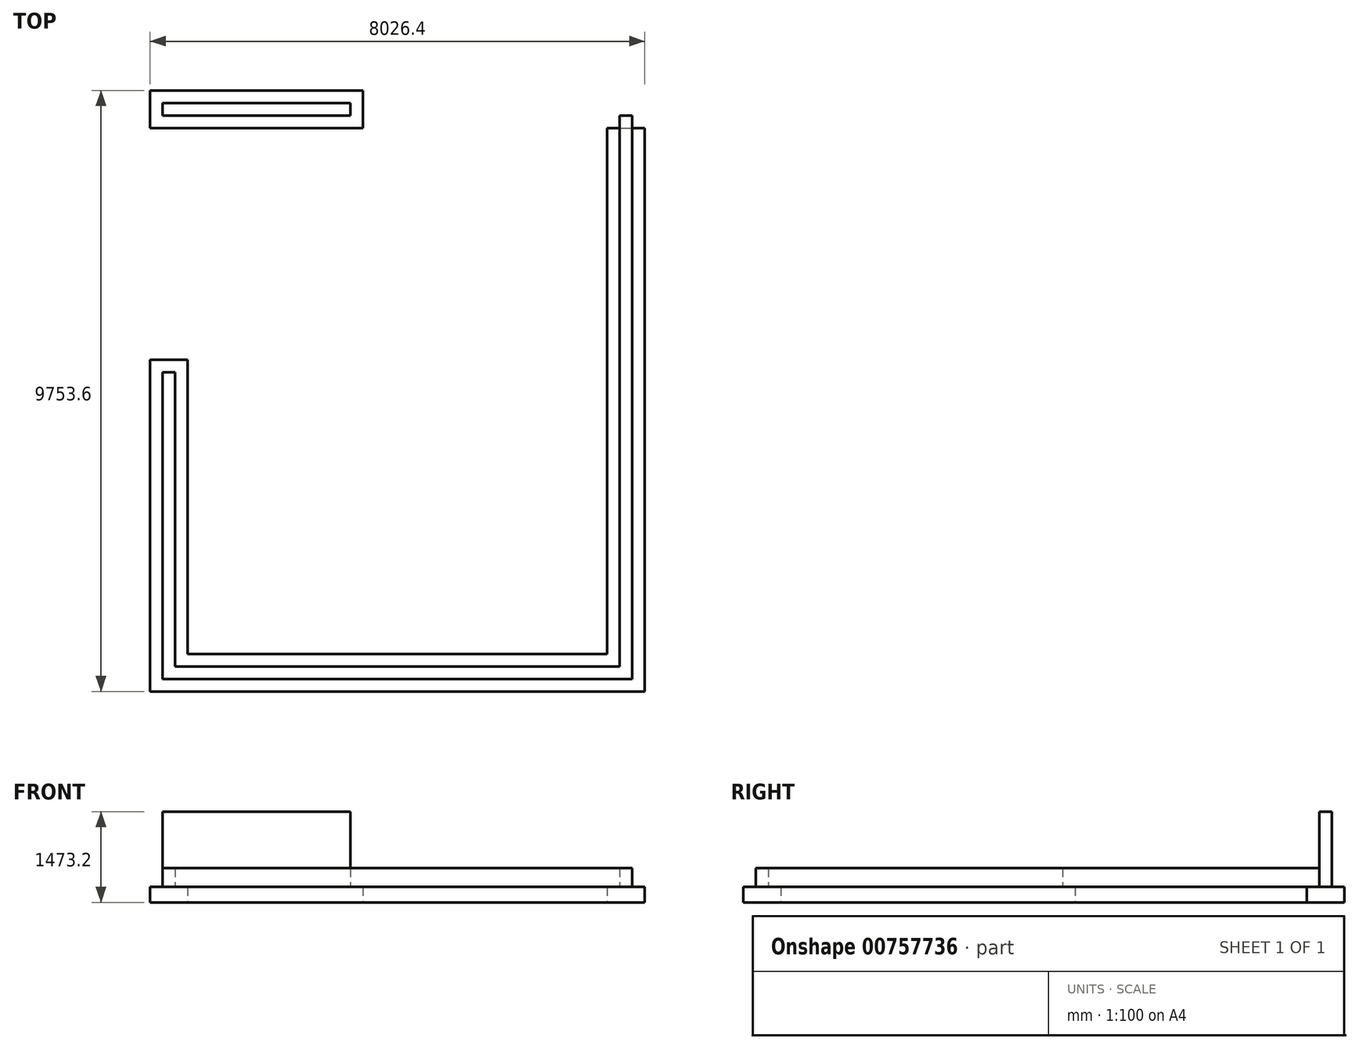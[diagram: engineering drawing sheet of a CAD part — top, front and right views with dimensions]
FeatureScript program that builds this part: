
annotation { "Feature Type Name" : "Feature", "Feature Type Description" : "" }
export const myFeature = defineFeature(function(context is Context, id is Id, definition is map)
    precondition{}
    {
        {
            var Q0;
            Q0=qCreatedBy(makeId("Top.planeOp"),FACE);
            var sketch = newSketch(context, id + "F0", { "sketchPlane" : qUnion([Q0])});
            skLineSegment(sketch, "E0", {"start": v(0, 0) * mm, "end": v(0, -609.6) * mm});
            skLineSegment(sketch, "E1", {"start": v(0, -609.6) * mm, "end": v(7416.8, -609.6) * mm});
            skLineSegment(sketch, "E2", {"start": v(7416.8, -609.6) * mm, "end": v(7416.8, -9144) * mm});
            skLineSegment(sketch, "E3", {"start": v(0, -4368.8) * mm, "end": v(0, -9753.6) * mm});
            skLineSegment(sketch, "E4", {"start": v(0, -9753.6) * mm, "end": v(8026.4, -9753.6) * mm});
            skLineSegment(sketch, "E5", {"start": v(8026.4, -9753.6) * mm, "end": v(8026.4, 0) * mm});
            skLineSegment(sketch, "E6", {"start": v(8026.4, 0) * mm, "end": v(0, 0) * mm});
            skLineSegment(sketch, "E7", {"start": v(0, -4368.8) * mm, "end": v(609.6, -4368.8) * mm});
            skLineSegment(sketch, "E8", {"start": v(609.6, -4368.8) * mm, "end": v(609.6, -9144) * mm});
            skLineSegment(sketch, "E9", {"start": v(609.6, -9144) * mm, "end": v(7416.8, -9144) * mm});
            skSolve(sketch);
        }
        {
            var Q0;
            Q0=makeQuery(id+"F0.imprint","IMPRINT",FACE,{"disambiguationData":[TD([[makeQuery(id+"F0.imprint","IMPRINT",EDGE,{"derivedFrom":sQuery(id+"F0.wireOp",EDGE,"E0")}),1.0]])]});
            extrude(context, id + "F1", {"entities" : qUnion([Q0]), "depth" : 254 * mm, "offsetDistance" : 25.4 * mm});
        }
        {
            var Q0;
            Q0=makeQuery(id+"F1.opExtrude","CAP_FACE",FACE,{"disambiguationData":[OSD([sQuery(id+"F0.wireOp",EDGE,"E0"),sQuery(id+"F0.wireOp",EDGE,"E1"),sQuery(id+"F0.wireOp",EDGE,"E2"),sQuery(id+"F0.wireOp",EDGE,"E3"),sQuery(id+"F0.wireOp",EDGE,"E4"),sQuery(id+"F0.wireOp",EDGE,"E5"),sQuery(id+"F0.wireOp",EDGE,"E6"),sQuery(id+"F0.wireOp",EDGE,"E7"),sQuery(id+"F0.wireOp",EDGE,"E8"),sQuery(id+"F0.wireOp",EDGE,"E9")])],"isStart":false});
            var sketch = newSketch(context, id + "F2", { "sketchPlane" : qUnion([Q0])});
            skLineSegment(sketch, "E10", {"start": v(203.2, -203.2) * mm, "end": v(203.2, -406.4) * mm});
            skLineSegment(sketch, "E11", {"start": v(203.2, -406.4) * mm, "end": v(3251.2, -406.4) * mm});
            skLineSegment(sketch, "E12", {"start": v(203.2, -203.2) * mm, "end": v(3251.2, -203.2) * mm});
            skLineSegment(sketch, "E13", {"start": v(3251.2, -203.2) * mm, "end": v(3251.2, -406.4) * mm});
            skLineSegment(sketch, "E14", {"start": v(7620, -406.4) * mm, "end": v(7620, -9347.2) * mm});
            skLineSegment(sketch, "E15", {"start": v(7620, -9347.2) * mm, "end": v(406.4, -9347.2) * mm});
            skLineSegment(sketch, "E16", {"start": v(406.4, -9347.2) * mm, "end": v(406.4, -4572) * mm});
            skLineSegment(sketch, "E17", {"start": v(406.4, -4572) * mm, "end": v(203.2, -4572) * mm});
            skLineSegment(sketch, "E18", {"start": v(203.2, -4572) * mm, "end": v(203.2, -9550.4) * mm});
            skLineSegment(sketch, "E19", {"start": v(203.2, -9550.4) * mm, "end": v(7823.2, -9550.4) * mm});
            skLineSegment(sketch, "E20", {"start": v(7823.2, -9550.4) * mm, "end": v(7823.2, -406.4) * mm});
            skLineSegment(sketch, "E21", {"start": v(7823.2, -406.4) * mm, "end": v(7620, -406.4) * mm});
            skSolve(sketch);
        }
        {
            var Q0;
            Q0 = qSketchRegion(id + "F2", true);
            extrude(context, id + "F3", {"entities" : qUnion([Q0]), "operationType" : NewBodyOperationType.ADD, "depth" : 304.8 * mm, "offsetDistance" : 25.4 * mm});
        }
        {
            var Q0;
            Q0=makeQuery(id+"F3.opExtrude","CAP_FACE",FACE,{"disambiguationData":[OSD([sQuery(id+"F2.wireOp",EDGE,"E10"),sQuery(id+"F2.wireOp",EDGE,"E11"),sQuery(id+"F2.wireOp",EDGE,"E12"),sQuery(id+"F2.wireOp",EDGE,"E13")])],"isStart":false});
            var sketch = newSketch(context, id + "F4", { "sketchPlane" : qUnion([Q0])});
            skLineSegment(sketch, "E22", {"start": v(203.2, -203.2) * mm, "end": v(3251.2, -203.2) * mm});
            skLineSegment(sketch, "E23", {"start": v(3251.2, -203.2) * mm, "end": v(3251.2, -406.4) * mm});
            skLineSegment(sketch, "E24", {"start": v(3251.2, -406.4) * mm, "end": v(203.2, -406.4) * mm});
            skLineSegment(sketch, "E25", {"start": v(203.2, -406.4) * mm, "end": v(203.2, -203.2) * mm});
            skSolve(sketch);
        }
        {
            var Q0;
            Q0 = qSketchRegion(id + "F4", true);
            extrude(context, id + "F5", {"entities" : qUnion([Q0]), "operationType" : NewBodyOperationType.ADD, "depth" : 914.4 * mm, "offsetDistance" : 25.4 * mm});
        }
        {
            var Q0;
            Q0=makeQuery(id+"F1.opExtrude","CAP_FACE",FACE,{"disambiguationData":[OSD([sQuery(id+"F0.wireOp",EDGE,"E0"),sQuery(id+"F0.wireOp",EDGE,"E1"),sQuery(id+"F0.wireOp",EDGE,"E2"),sQuery(id+"F0.wireOp",EDGE,"E3"),sQuery(id+"F0.wireOp",EDGE,"E4"),sQuery(id+"F0.wireOp",EDGE,"E5"),sQuery(id+"F0.wireOp",EDGE,"E6"),sQuery(id+"F0.wireOp",EDGE,"E7"),sQuery(id+"F0.wireOp",EDGE,"E8"),sQuery(id+"F0.wireOp",EDGE,"E9")])],"isStart":true});
            var sketch = newSketch(context, id + "F6", { "sketchPlane" : qUnion([Q0])});
            skLineSegment(sketch, "E26", {"start": v(8026.4, 0) * mm, "end": v(3454.4, 0) * mm});
            skLineSegment(sketch, "E27", {"start": v(3454.4, 0) * mm, "end": v(3454.4, 609.6) * mm});
            skLineSegment(sketch, "E28", {"start": v(3454.4, 609.6) * mm, "end": v(8026.4, 609.6) * mm});
            skLineSegment(sketch, "E29", {"start": v(8026.4, 609.6) * mm, "end": v(8026.4, 0) * mm});
            skSolve(sketch);
        }
        {
            var Q0;
            Q0 = qSketchRegion(id + "F6", true);
            extrude(context, id + "F7", {"entities" : qUnion([Q0]), "operationType" : NewBodyOperationType.REMOVE, "oppositeDirection" : true, "depth" : 254 * mm, "offsetDistance" : 25.4 * mm});
        }
    });
